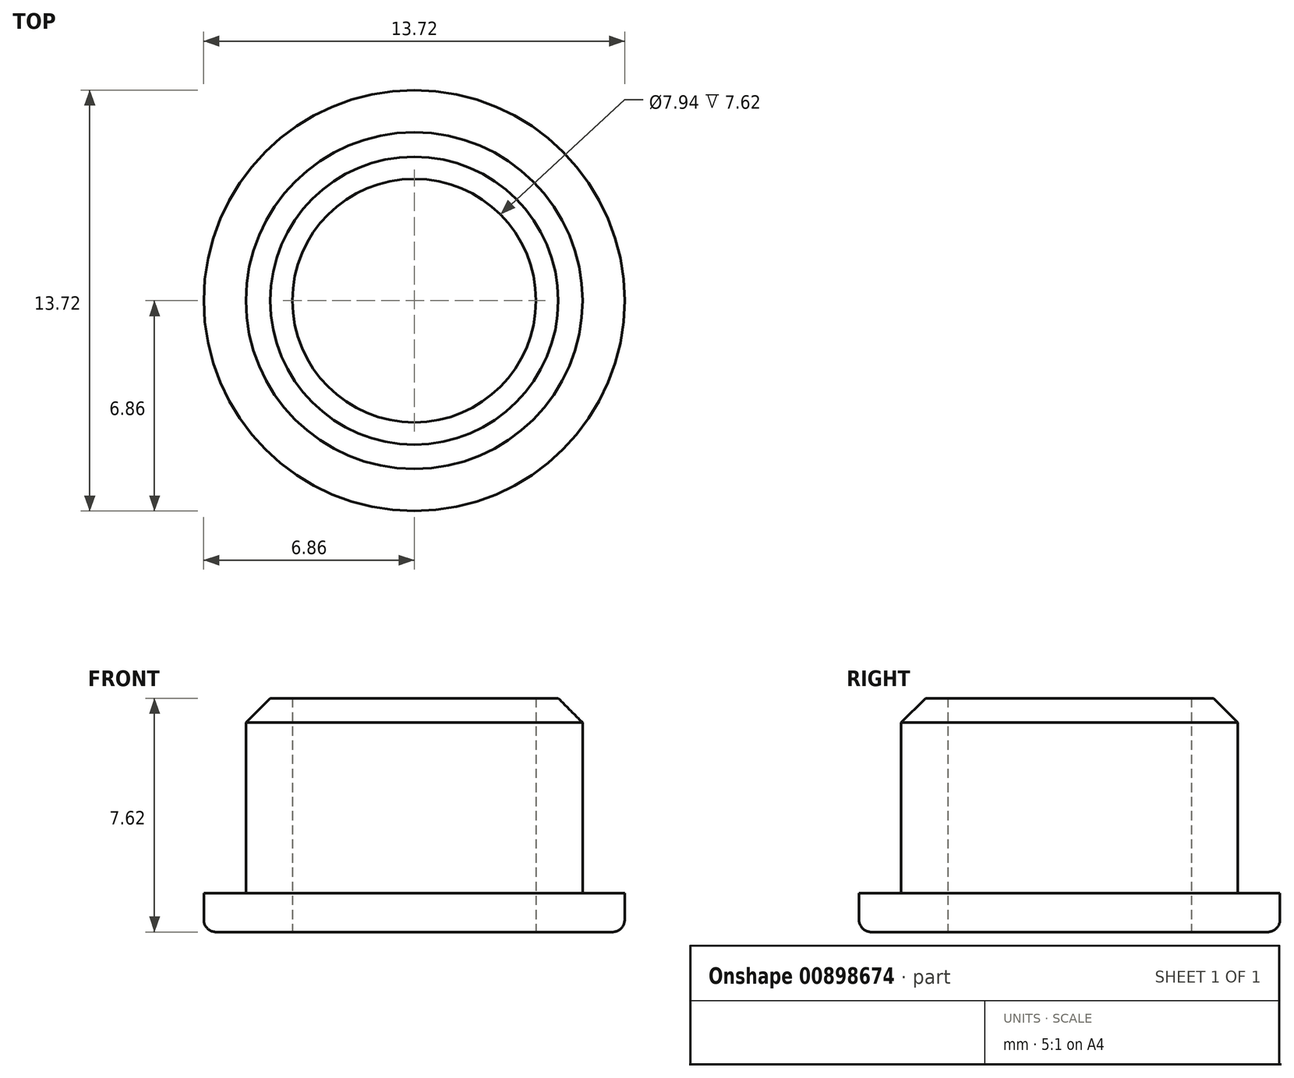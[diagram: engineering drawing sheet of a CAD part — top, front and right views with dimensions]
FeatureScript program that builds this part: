
annotation { "Feature Type Name" : "Feature", "Feature Type Description" : "" }
export const myFeature = defineFeature(function(context is Context, id is Id, definition is map)
    precondition{}
    {
        {
            var Q0;
            Q0=qCreatedBy(makeId("Top.planeOp"),FACE);
            var sketch = newSketch(context, id + "F0", { "sketchPlane" : qUnion([Q0])});
            skCircle(sketch, "E0", {"center": v(0, 0) * mm, "radius": 6.86 * mm});
            skSolve(sketch);
        }
        {
            var Q0;
            Q0 = qSketchRegion(id + "F0", true);
            extrude(context, id + "F1", {"entities" : qUnion([Q0]), "depth" : 1.27 * mm, "offsetDistance" : 25.4 * mm});
        }
        {
            var Q0;
            Q0=makeQuery(id+"F1.opExtrude","CAP_FACE",FACE,{"disambiguationData":[OSD([sQuery(id+"F0.wireOp",EDGE,"E0")])],"isStart":false});
            var sketch = newSketch(context, id + "F2", { "sketchPlane" : qUnion([Q0])});
            skCircle(sketch, "E1", {"center": v(0, 0) * mm, "radius": 5.49 * mm});
            skSolve(sketch);
        }
        {
            var Q0;
            Q0 = qSketchRegion(id + "F2", true);
            extrude(context, id + "F3", {"entities" : qUnion([Q0]), "operationType" : NewBodyOperationType.ADD, "depth" : 6.35 * mm, "offsetDistance" : 25.4 * mm});
        }
        {
            var Q0;
            Q0=qCreatedBy(makeId("Top.planeOp"),FACE);
            var sketch = newSketch(context, id + "F4", { "sketchPlane" : qUnion([Q0])});
            skCircle(sketch, "E2", {"center": v(0, 0) * mm, "radius": 3.97 * mm});
            skSolve(sketch);
        }
        {
            var Q0;
            Q0 = qSketchRegion(id + "F4", true);
            extrude(context, id + "F5", {"entities" : qUnion([Q0]), "operationType" : NewBodyOperationType.REMOVE, "depth" : 25.4 * mm, "offsetDistance" : 25.4 * mm});
        }
        {
            var Q0;
            Q0=makeQuery(id+"F3.opExtrude","CAP_EDGE",EDGE,{"disambiguationData":[OSD([sQuery(id+"F2.wireOp",EDGE,"E1")])],"isStart":false});
            var Q1;
            Q1=makeQuery(id+"F5.boolean.opBoolean","COPY",EDGE,{"derivedFrom":makeQuery(id+"F5.opExtrude","CAP_EDGE",EDGE,{"disambiguationData":[OSD([sQuery(id+"F4.wireOp",EDGE,"E2")])],"isStart":true})});
            chamfer(context, id + "F6", {"entities" : qUnion([Q0, Q1]), "width" : 0.8 * mm, "tangentPropagation" : true});
        }
        {
            var Q0;
            Q0=makeQuery(id+"F1.opExtrude","CAP_EDGE",EDGE,{"disambiguationData":[OSD([sQuery(id+"F0.wireOp",EDGE,"E0")])],"isStart":true});
            fillet(context, id + "F7", {"entities" : qUnion([Q0]), "radius" : 0.4 * mm, "tangentPropagation" : true, "allowEdgeOverflow" : false});
        }
    });
